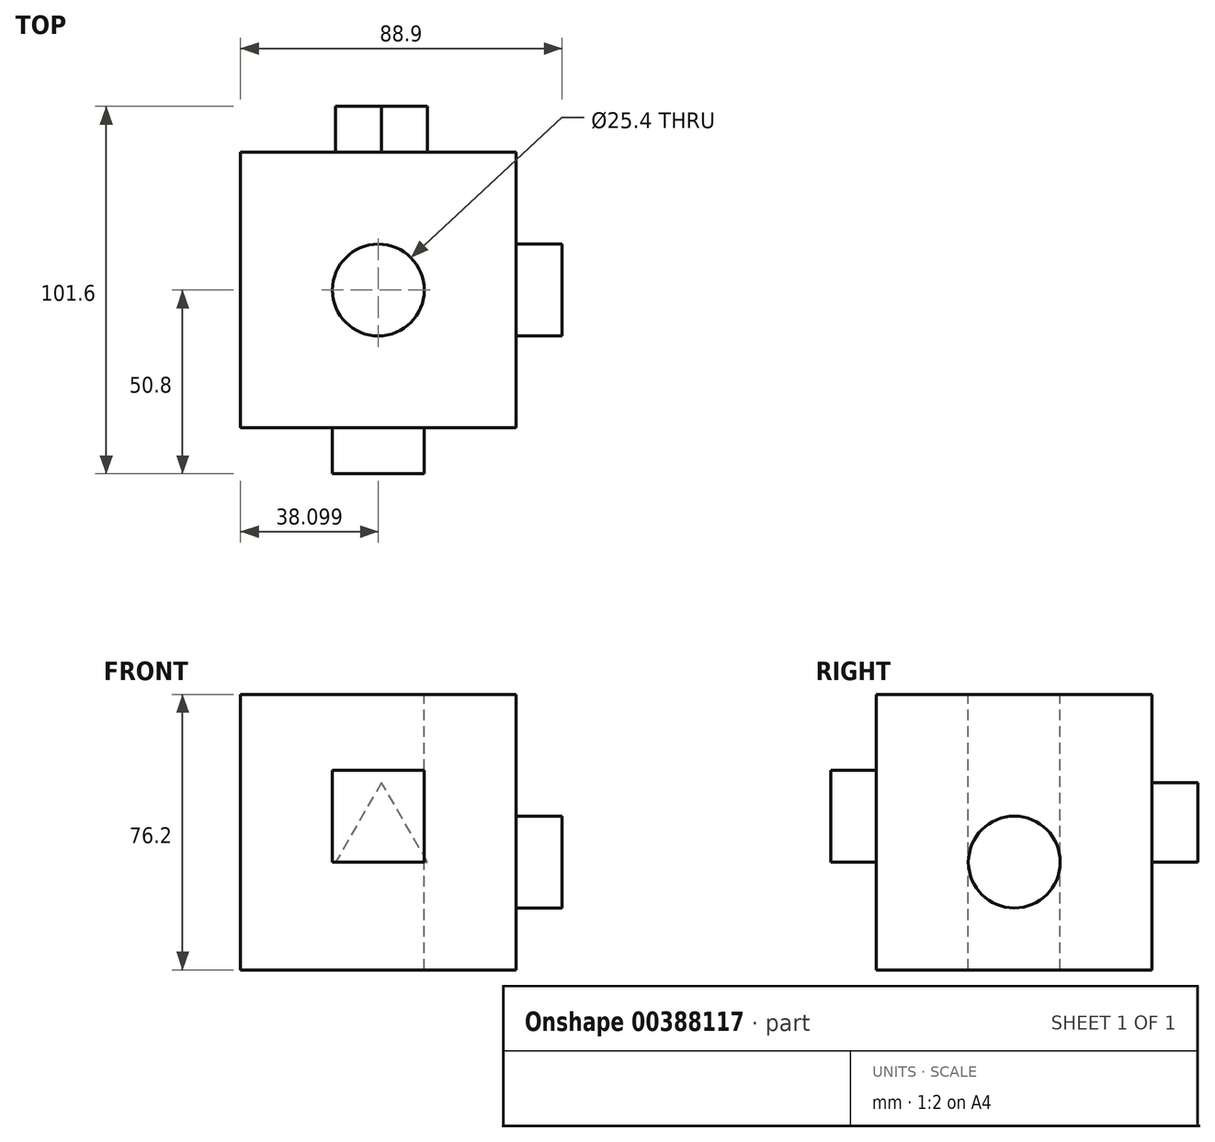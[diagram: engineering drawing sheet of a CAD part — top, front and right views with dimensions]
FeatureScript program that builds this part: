
annotation { "Feature Type Name" : "Feature", "Feature Type Description" : "" }
export const myFeature = defineFeature(function(context is Context, id is Id, definition is map)
    precondition{}
    {
        {
            var Q0;
            Q0=qCreatedBy(makeId("Front.planeOp"),FACE);
            var sketch = newSketch(context, id + "F0", { "sketchPlane" : qUnion([Q0])});
            skLineSegment(sketch, "E0.bottom", {"start": v(-34.31, 46.4) * mm, "end": v(41.89, 46.4) * mm});
            skLineSegment(sketch, "E0.top", {"start": v(-34.31, -29.8) * mm, "end": v(41.89, -29.8) * mm});
            skLineSegment(sketch, "E0.left", {"start": v(-34.31, 46.4) * mm, "end": v(-34.31, -29.8) * mm});
            skLineSegment(sketch, "E0.right", {"start": v(41.89, 46.4) * mm, "end": v(41.89, -29.8) * mm});
            skSolve(sketch);
        }
        {
            var Q0;
            Q0=makeQuery(id+"F0.imprint","IMPRINT",FACE,{"disambiguationData":[TD([[makeQuery(id+"F0.imprint","IMPRINT",EDGE,{"derivedFrom":sQuery(id+"F0.wireOp",EDGE,"E0.bottom")}),-1.0]])]});
            extrude(context, id + "F1", {"entities" : qUnion([Q0]), "depth" : 76.2 * mm});
        }
        {
            var Q0;
            Q0=makeQuery(id+"F1.opExtrude","SWEPT_FACE",FACE,{"disambiguationData":[OSD([sQuery(id+"F0.wireOp",EDGE,"E0.bottom")])]});
            var sketch = newSketch(context, id + "F2", { "sketchPlane" : qUnion([Q0])});
            skPoint(sketch, "E1", {"position": v(3.79, -38.1) * mm});
            skSolve(sketch);
        }
        {
            var Q0;
            Q0=sQuery(id+"F2.wireOp",VERTEX,"E1");
            var Q1;
            Q1=makeQuery(id+"F1.opExtrude","SWEPT_BODY",BODY,{"disambiguationData":[OSD([sQuery(id+"F0.wireOp",EDGE,"E0.bottom"),sQuery(id+"F0.wireOp",EDGE,"E0.top"),sQuery(id+"F0.wireOp",EDGE,"E0.left"),sQuery(id+"F0.wireOp",EDGE,"E0.right")])]});
            hole(context, id + "F3", {"style" : HoleStyle.SIMPLE, "endStyle" : HoleEndStyle.THROUGH, "holeDiameter" : 25.4 * mm, "isTappedThrough" : true, "tappedDepth" : 12.7 * mm, "tapClearance" : 3, "locations" : qUnion([Q0]), "scope" : qUnion([Q1])});
        }
        {
            var Q0;
            Q0=makeQuery(id+"F1.opExtrude","CAP_FACE",FACE,{"disambiguationData":[OSD([sQuery(id+"F0.wireOp",EDGE,"E0.bottom"),sQuery(id+"F0.wireOp",EDGE,"E0.top"),sQuery(id+"F0.wireOp",EDGE,"E0.left"),sQuery(id+"F0.wireOp",EDGE,"E0.right")])],"isStart":false});
            var sketch = newSketch(context, id + "F4", { "sketchPlane" : qUnion([Q0])});
            skLineSegment(sketch, "E2.bottom", {"start": v(-8.91, 25.4) * mm, "end": v(16.49, 25.4) * mm});
            skLineSegment(sketch, "E2.top", {"start": v(-8.91, 0) * mm, "end": v(16.49, 0) * mm});
            skLineSegment(sketch, "E2.left", {"start": v(-8.91, 25.4) * mm, "end": v(-8.91, 0) * mm});
            skLineSegment(sketch, "E2.right", {"start": v(16.49, 25.4) * mm, "end": v(16.49, 0) * mm});
            skSolve(sketch);
        }
        {
            var Q0;
            Q0=makeQuery(id+"F4.imprint","IMPRINT",FACE,{"disambiguationData":[TD([[makeQuery(id+"F4.imprint","IMPRINT",EDGE,{"derivedFrom":sQuery(id+"F4.wireOp",EDGE,"E2.bottom")}),-1.0]])]});
            extrude(context, id + "F5", {"entities" : qUnion([Q0]), "operationType" : NewBodyOperationType.ADD, "depth" : 12.7 * mm});
        }
        {
            var Q0;
            Q0=makeQuery(id+"F1.opExtrude","SWEPT_FACE",FACE,{"disambiguationData":[OSD([sQuery(id+"F0.wireOp",EDGE,"E0.right")])]});
            var sketch = newSketch(context, id + "F6", { "sketchPlane" : qUnion([Q0])});
            skCircle(sketch, "E3", {"center": v(-38.1, 0) * mm, "radius": 12.7 * mm});
            skSolve(sketch);
        }
        {
            var Q0;
            Q0=makeQuery(id+"F6.imprint","IMPRINT",FACE,{"disambiguationData":[TD([[makeQuery(id+"F6.imprint","IMPRINT",EDGE,{"derivedFrom":sQuery(id+"F6.wireOp",EDGE,"E3")}),1.0]])]});
            extrude(context, id + "F7", {"entities" : qUnion([Q0]), "operationType" : NewBodyOperationType.ADD, "depth" : 12.7 * mm});
        }
        {
            var Q0;
            Q0=makeQuery(id+"F1.opExtrude","CAP_FACE",FACE,{"disambiguationData":[OSD([sQuery(id+"F0.wireOp",EDGE,"E0.bottom"),sQuery(id+"F0.wireOp",EDGE,"E0.top"),sQuery(id+"F0.wireOp",EDGE,"E0.left"),sQuery(id+"F0.wireOp",EDGE,"E0.right")])],"isStart":true});
            var sketch = newSketch(context, id + "F8", { "sketchPlane" : qUnion([Q0])});
            skCircle(sketch, "E4.cCircle", {"center": v(-4.7, 7.33) * mm, "radius": 7.33 * mm, "construction": true});
            skLineSegment(sketch, "E4.0", {"start": v(8, 0) * mm, "end": v(-17.4, 0) * mm});
            skLineSegment(sketch, "E4.1", {"start": v(-17.4, 0) * mm, "end": v(-4.7, 22) * mm});
            skLineSegment(sketch, "E4.2", {"start": v(-4.7, 22) * mm, "end": v(8, 0) * mm});
            skPoint(sketch, "E4.0.midPoint", {"position": v(-4.7, 0) * mm});
            skSolve(sketch);
        }
        {
            var Q0;
            Q0=makeQuery(id+"F8.imprint","IMPRINT",FACE,{"disambiguationData":[TD([[makeQuery(id+"F8.imprint","IMPRINT",EDGE,{"derivedFrom":sQuery(id+"F8.wireOp",EDGE,"E4.0")}),-1.0]])]});
            var Q1;
            Q1=makeQuery(id+"F5.opExtrude","CAP_FACE",FACE,{"disambiguationData":[OSD([sQuery(id+"F4.wireOp",EDGE,"E2.bottom"),sQuery(id+"F4.wireOp",EDGE,"E2.top"),sQuery(id+"F4.wireOp",EDGE,"E2.left"),sQuery(id+"F4.wireOp",EDGE,"E2.right")])],"isStart":false});
            extrude(context, id + "F9", {"entities" : qUnion([Q0, Q1]), "operationType" : NewBodyOperationType.ADD, "depth" : 12.7 * mm});
        }
    });
